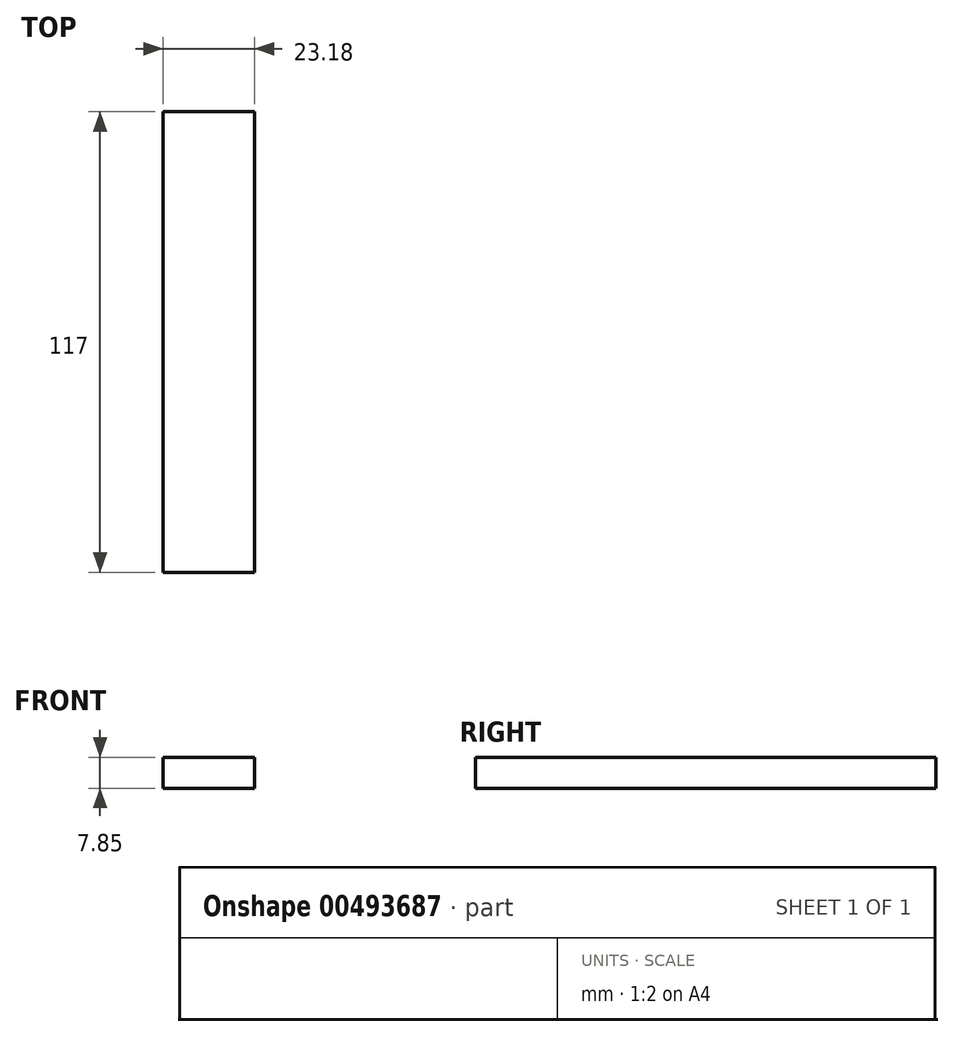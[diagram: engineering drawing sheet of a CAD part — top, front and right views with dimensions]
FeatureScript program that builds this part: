
annotation { "Feature Type Name" : "Feature", "Feature Type Description" : "" }
export const myFeature = defineFeature(function(context is Context, id is Id, definition is map)
    precondition{}
    {
        {
            var Q0;
            Q0=qCreatedBy(makeId("Top.planeOp"),FACE);
            var sketch = newSketch(context, id + "F0", { "sketchPlane" : qUnion([Q0])});
            skLineSegment(sketch, "E0.bottom", {"start": v(11.59, -58.5) * mm, "end": v(-11.59, -58.5) * mm});
            skLineSegment(sketch, "E0.top", {"start": v(11.59, 58.5) * mm, "end": v(-11.59, 58.5) * mm});
            skLineSegment(sketch, "E0.left", {"start": v(11.59, -58.5) * mm, "end": v(11.59, 58.5) * mm});
            skLineSegment(sketch, "E0.right", {"start": v(-11.59, -58.5) * mm, "end": v(-11.59, 58.5) * mm});
            skPoint(sketch, "E0.middle", {"position": v(0, 0) * mm});
            skSolve(sketch);
        }
        {
            var Q0;
            Q0 = qSketchRegion(id + "F0", true);
            extrude(context, id + "F1", {"entities" : qUnion([Q0]), "depth" : 7.85 * mm});
        }
    });
